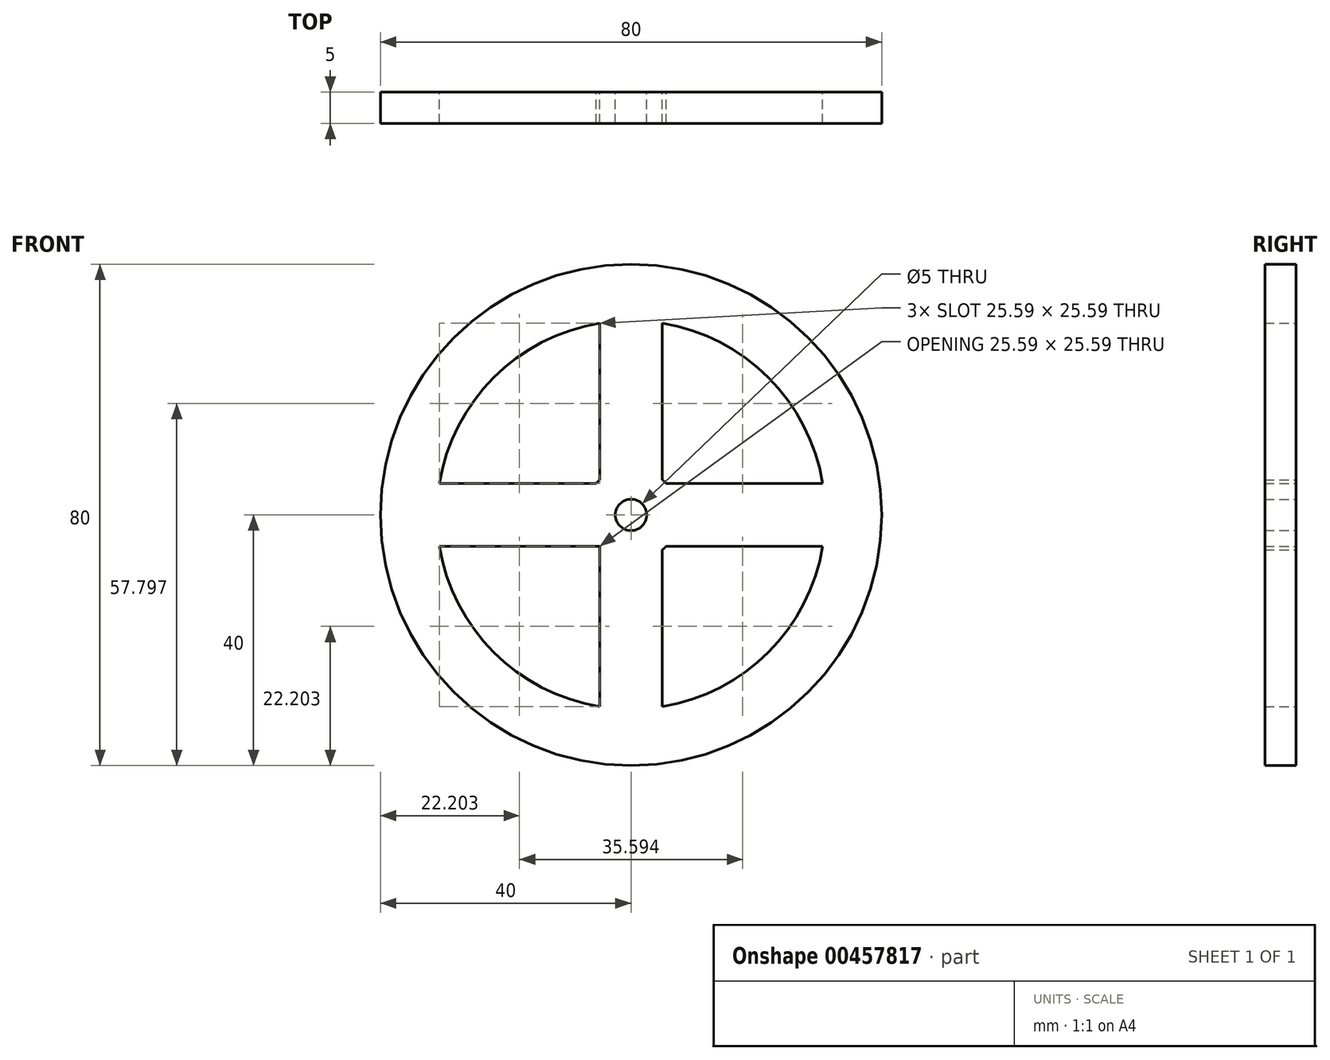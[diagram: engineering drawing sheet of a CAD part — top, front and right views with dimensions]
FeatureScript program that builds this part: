
annotation { "Feature Type Name" : "Feature", "Feature Type Description" : "" }
export const myFeature = defineFeature(function(context is Context, id is Id, definition is map)
    precondition{}
    {
        {
            var Q0;
            Q0=qCreatedBy(makeId("Front.planeOp"),FACE);
            var sketch = newSketch(context, id + "F0", { "sketchPlane" : qUnion([Q0])});
            skCircle(sketch, "E0", {"center": v(0, 0) * mm, "radius": 40 * mm});
            skArc(sketch, "E1", {"start": v(-5, 30.6) * mm, "mid": v(-21.92, 21.92) * mm, "end": v(-30.6, 5) * mm});
            skArc(sketch, "E2", {"start": v(5.6, 5) * mm, "mid": v(5.3, 5.3) * mm, "end": v(5, 5.6) * mm});
            skCircle(sketch, "E3", {"center": v(0, 0) * mm, "radius": 2.5 * mm});
            skLineSegment(sketch, "E4", {"start": v(0, 0) * mm, "end": v(40, 0) * mm});
            skLineSegment(sketch, "E5", {"start": v(0, 0) * mm, "end": v(0, 31) * mm});
            skLineSegment(sketch, "E6", {"start": v(0, 0) * mm, "end": v(-40, 0) * mm});
            skLineSegment(sketch, "E7", {"start": v(0, 0) * mm, "end": v(0, -40) * mm});
            skLineSegment(sketch, "E8.0", {"start": v(5, 5.6) * mm, "end": v(5, 30.6) * mm});
            skLineSegment(sketch, "E9.0", {"start": v(-5.6, 5) * mm, "end": v(-30.6, 5) * mm});
            skLineSegment(sketch, "E10.0", {"start": v(-5, -5) * mm, "end": v(-30.6, -5) * mm});
            skLineSegment(sketch, "E11.0", {"start": v(5, -5) * mm, "end": v(30.6, -5) * mm});
            skLineSegment(sketch, "E12.0", {"start": v(5.6, 5) * mm, "end": v(30.6, 5) * mm});
            skLineSegment(sketch, "E13.0", {"start": v(-5, -5) * mm, "end": v(-5, -30.6) * mm});
            skLineSegment(sketch, "E14.0", {"start": v(5, -5.6) * mm, "end": v(5, -30.6) * mm});
            skArc(sketch, "E15.trimOffspring", {"start": v(30.6, 5) * mm, "mid": v(21.92, 21.92) * mm, "end": v(5, 30.6) * mm});
            skArc(sketch, "E16.trimOffspring", {"start": v(5, -30.6) * mm, "mid": v(21.92, -21.92) * mm, "end": v(30.6, -5) * mm});
            skArc(sketch, "E17.trimOffspring", {"start": v(-30.6, -5) * mm, "mid": v(-21.92, -21.92) * mm, "end": v(-5, -30.6) * mm});
            skArc(sketch, "E18.trimOffspring", {"start": v(5, -5.6) * mm, "mid": v(5.3, -5.3) * mm, "end": v(5.6, -5) * mm});
            skArc(sketch, "E19.trimOffspring", {"start": v(-5.6, -5) * mm, "mid": v(-5.3, -5.3) * mm, "end": v(-5, -5.6) * mm});
            skArc(sketch, "E20.trimOffspring", {"start": v(-5, 5.6) * mm, "mid": v(-5.3, 5.3) * mm, "end": v(-5.6, 5) * mm});
            skLineSegment(sketch, "E21.trimOffspring", {"start": v(-5, 5.6) * mm, "end": v(-5, 30.6) * mm});
            skSolve(sketch);
        }
        {
            var Q0;
            Q0 = qSketchRegion(id + "F0", true);
            extrude(context, id + "F1", {"entities" : qUnion([Q0]), "endBound" : BoundingType.SYMMETRIC, "depth" : 5 * mm});
        }
    });
